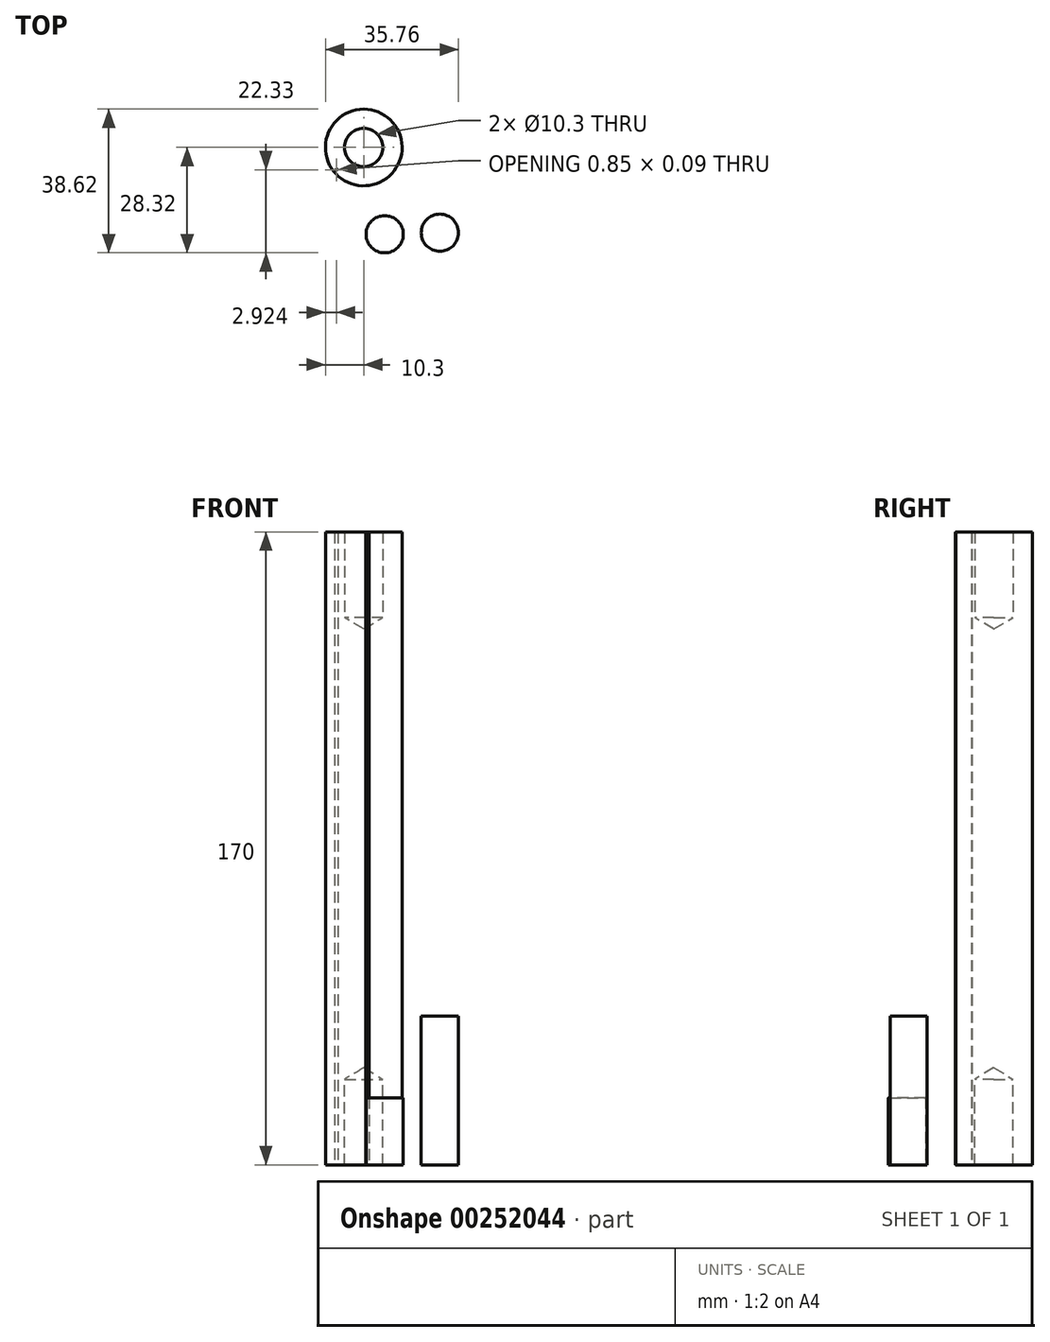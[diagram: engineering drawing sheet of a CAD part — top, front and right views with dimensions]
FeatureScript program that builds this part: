
annotation { "Feature Type Name" : "Feature", "Feature Type Description" : "" }
export const myFeature = defineFeature(function(context is Context, id is Id, definition is map)
    precondition{}
    {
        {
            var Q0;
            Q0=qCreatedBy(makeId("Top.planeOp"),FACE);
            var sketch = newSketch(context, id + "F0", { "sketchPlane" : qUnion([Q0])});
            skCircle(sketch, "E0", {"center": v(0, 0) * mm, "radius": 10.3 * mm});
            skPoint(sketch, "E1.left.start.orphan", {"position": v(35.27, 0) * mm});
            skCircle(sketch, "E2", {"center": v(20.46, -22.9) * mm, "radius": 5 * mm});
            skPoint(sketch, "E3.left.start.orphan", {"position": v(17.37, 7.63) * mm});
            skArc(sketch, "E4", {"start": v(1.46, -10.2) * mm, "mid": v(1.03, -10.22) * mm, "end": v(0.6, -10.28) * mm});
            skPoint(sketch, "E5.center.orphan", {"position": v(-23.67, 0) * mm});
            skArc(sketch, "E6", {"start": v(-8.34, -6.05) * mm, "mid": v(-7.64, -6.02) * mm, "end": v(-6.95, -5.95) * mm});
            skPoint(sketch, "E7.left.start.orphan", {"position": v(26.86, 4.25) * mm});
            skCircle(sketch, "E8", {"center": v(5.64, -23.32) * mm, "radius": 5 * mm});
            skPoint(sketch, "E9.left.start.orphan", {"position": v(8.96, 11.88) * mm});
            skArc(sketch, "E10", {"start": v(-6.95, -5.95) * mm, "mid": v(-7.38, -5.97) * mm, "end": v(-7.8, -6.03) * mm});
            skPoint(sketch, "E11.center.orphan", {"position": v(-32.08, 4.25) * mm});
            skSolve(sketch);
        }
        {
            var Q0;
            Q0=makeQuery(id+"F0.imprint","IMPRINT",FACE,{"disambiguationData":[TD([[makeQuery(id+"F0.imprint","IMPRINT",EDGE,{"derivedFrom":sQuery(id+"F0.wireOp",EDGE,"E0")}),1.0]])]});
            var Q1;
            Q1=makeQuery(id+"F0.imprint","IMPRINT",FACE,{"disambiguationData":[TD([[makeQuery(id+"F0.imprint","IMPRINT",EDGE,{"derivedFrom":sQuery(id+"F0.wireOp",EDGE,"37e82010-eb41-4067-ba32-22d23ce87656")}),1.0]])]});
            extrude(context, id + "F4", {"entities" : qUnion([Q0, Q1]), "depth" : 170 * mm});
        }
        {
            var Q0;
            Q0=makeQuery(id+"F0.imprint","IMPRINT",FACE,{"disambiguationData":[TD([[makeQuery(id+"F0.imprint","IMPRINT",EDGE,{"derivedFrom":sQuery(id+"F0.wireOp",EDGE,"E2")}),1.0]])]});
            extrude(context, id + "F5", {"entities" : qUnion([Q0]), "depth" : 40 * mm});
        }
        {
            var Q0;
            Q0=sQuery(id+"F0.wireOp",VERTEX,"E0.center");
            var Q1;
            Q1=makeQuery(id+"F4.opExtrude","SWEPT_BODY",BODY,{"disambiguationData":[OSD([sQuery(id+"F0.wireOp",EDGE,"E0")])]});
            hole(context, id + "F6", {"style" : HoleStyle.SIMPLE, "endStyle" : HoleEndStyle.BLIND, "oppositeDirection" : true, "standardTappedOrClearance" : lookupTablePath({ "standard" : "ANSI" }), "standardBlindInLast" : lookupTablePath({ "standard" : "ANSI" }), "holeDiameter" : 10.3 * mm, "holeDepth" : 23 * mm, "tappedDepth" : 12 * mm, "tapClearance" : 3, "locations" : qUnion([Q0]), "scope" : qUnion([Q1])});
        }
        {
            var Q0;
            Q0=makeQuery(id+"F0.imprint","IMPRINT",FACE,{"disambiguationData":[TD([[makeQuery(id+"F0.imprint","IMPRINT",EDGE,{"derivedFrom":sQuery(id+"F0.wireOp",EDGE,"E8")}),1.0]])]});
            extrude(context, id + "F1", {"entities" : qUnion([Q0]), "depth" : 18 * mm});
        }
        {
            var Q0;
            Q0=makeQuery(id+"F4.opExtrude","CAP_FACE",FACE,{"disambiguationData":[OSD([sQuery(id+"F0.wireOp",EDGE,"E0"),sQuery(id+"F0.wireOp",EDGE,"E4"),sQuery(id+"F0.wireOp",EDGE,"E6"),sQuery(id+"F0.wireOp",EDGE,"E10")])],"isStart":false});
            var sketch = newSketch(context, id + "F2", { "sketchPlane" : qUnion([Q0])});
            skLineSegment(sketch, "E12", {"start": v(0, 10.3) * mm, "end": v(0, -10.3) * mm, "construction": true});
            skPoint(sketch, "E13", {"position": v(0, 0) * mm});
            skSolve(sketch);
        }
        {
            var Q0;
            Q0=sQuery(id+"F2.wireOp",VERTEX,"E13");
            var Q1;
            Q1=makeQuery(id+"F4.opExtrude","SWEPT_BODY",BODY,{"disambiguationData":[OSD([sQuery(id+"F0.wireOp",EDGE,"E0"),sQuery(id+"F0.wireOp",EDGE,"E4"),sQuery(id+"F0.wireOp",EDGE,"E6"),sQuery(id+"F0.wireOp",EDGE,"E10")])]});
            hole(context, id + "F3", {"style" : HoleStyle.SIMPLE, "endStyle" : HoleEndStyle.BLIND, "holeDiameter" : 10.3 * mm, "holeDepth" : 23 * mm, "tappedDepth" : 12 * mm, "tapClearance" : 3, "locations" : qUnion([Q0]), "scope" : qUnion([Q1])});
        }
    });
